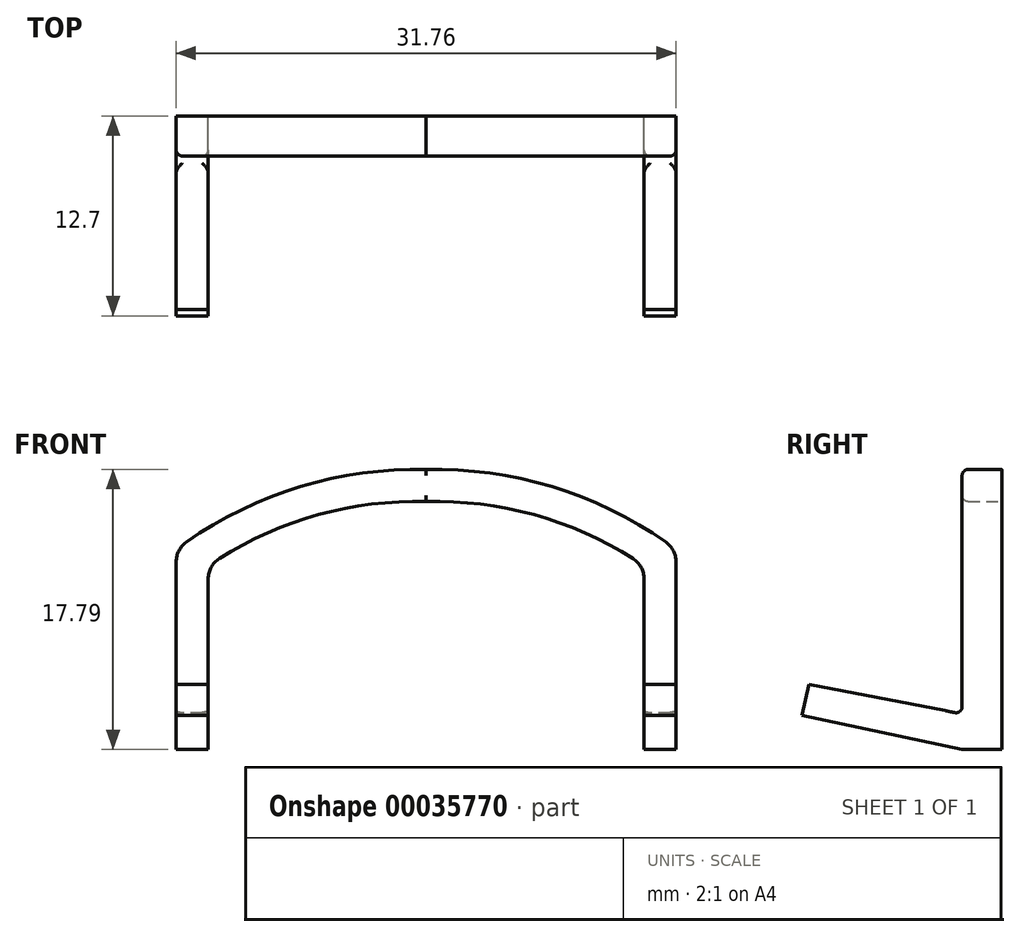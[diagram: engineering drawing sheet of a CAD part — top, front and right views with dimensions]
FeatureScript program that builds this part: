
annotation { "Feature Type Name" : "Feature", "Feature Type Description" : "" }
export const myFeature = defineFeature(function(context is Context, id is Id, definition is map)
    precondition{}
    {
        {
            var Q0;
            Q0=qCreatedBy(makeId("Front.planeOp"),FACE);
            var sketch = newSketch(context, id + "F0", { "sketchPlane" : qUnion([Q0])});
            skLineSegment(sketch, "E0", {"start": v(0, 0) * mm, "end": v(0, 38.1) * mm, "construction": true});
            skLineSegment(sketch, "E1", {"start": v(-15.88, 11.92) * mm, "end": v(-15.88, 0) * mm});
            skLineSegment(sketch, "E2", {"start": v(-15.88, 0) * mm, "end": v(-13.84, 0) * mm});
            skLineSegment(sketch, "E3", {"start": v(-13.84, 0) * mm, "end": v(-13.84, 10.84) * mm});
            skArc(sketch, "E4", {"start": v(0, 17.78) * mm, "mid": v(-7.98, 16.7) * mm, "end": v(-15.23, 13.17) * mm});
            skArc(sketch, "E5.0", {"start": v(0, 15.75) * mm, "mid": v(-6.84, 14.91) * mm, "end": v(-13.13, 12.12) * mm});
            skArc(sketch, "E6.filletArc", {"start": v(-13.13, 12.12) * mm, "mid": v(-13.65, 11.57) * mm, "end": v(-13.84, 10.84) * mm});
            skPoint(sketch, "E7.visualSharp", {"position": v(-15.88, 12.7) * mm});
            skArc(sketch, "E7.filletArc", {"start": v(-15.23, 13.17) * mm, "mid": v(-15.7, 12.63) * mm, "end": v(-15.88, 11.92) * mm});
            skArc(sketch, "E8.MirrorCS", {"start": v(13.13, 12.12) * mm, "mid": v(13.65, 11.57) * mm, "end": v(13.84, 10.84) * mm});
            skArc(sketch, "E9.MirrorCS", {"start": v(15.23, 13.17) * mm, "mid": v(15.7, 12.63) * mm, "end": v(15.88, 11.92) * mm});
            skLineSegment(sketch, "E10.MirrorCS", {"start": v(15.88, 0) * mm, "end": v(13.84, 0) * mm});
            skArc(sketch, "E11.MirrorCS", {"start": v(0, 17.78) * mm, "mid": v(7.98, 16.7) * mm, "end": v(15.23, 13.17) * mm});
            skPoint(sketch, "E12.MirrorP", {"position": v(15.88, 12.7) * mm});
            skLineSegment(sketch, "E13.MirrorCS", {"start": v(15.88, 11.92) * mm, "end": v(15.88, 0) * mm});
            skLineSegment(sketch, "E14.MirrorCS", {"start": v(13.84, 0) * mm, "end": v(13.84, 10.84) * mm});
            skArc(sketch, "E15.MirrorCS", {"start": v(0, 15.75) * mm, "mid": v(6.84, 14.91) * mm, "end": v(13.13, 12.12) * mm});
            skSolve(sketch);
        }
        {
            var Q0;
            Q0 = qSketchRegion(id + "F0", true);
            extrude(context, id + "F1", {"entities" : qUnion([Q0]), "depth" : 2.54 * mm});
        }
        {
            var Q0;
            Q0=qCreatedBy(makeId("Right.planeOp"),FACE);
            var sketch = newSketch(context, id + "F2", { "sketchPlane" : qUnion([Q0])});
            skLineSegment(sketch, "E16.0", {"start": v(-2.54, 2.25) * mm, "end": v(-2.54, 0) * mm});
            skLineSegment(sketch, "E17", {"start": v(-2.54, 0) * mm, "end": v(-12.7, 2.16) * mm});
            skLineSegment(sketch, "E18", {"start": v(-2.54, 2.25) * mm, "end": v(-12.28, 4.15) * mm});
            skLineSegment(sketch, "E19", {"start": v(-12.28, 4.15) * mm, "end": v(-12.7, 2.16) * mm});
            skPoint(sketch, "E20.orphan", {"position": v(-2.54, 11.92) * mm});
            skLineSegment(sketch, "E21", {"start": v(-2.54, 0) * mm, "end": v(-11.31, 0) * mm, "construction": true});
            skSolve(sketch);
        }
        {
            var Q0;
            Q0 = qSketchRegion(id + "F2", true);
            var Q1;
            Q1=makeQuery(id+"F1.opExtrude","SWEPT_FACE",FACE,{"disambiguationData":[OSD([sQuery(id+"F0.wireOp",EDGE,"E13.MirrorCS")])]});
            var Q2;
            Q2=makeQuery(id+"F1.opExtrude","SWEPT_FACE",FACE,{"disambiguationData":[OSD([sQuery(id+"F0.wireOp",EDGE,"E1")])]});
            extrude(context, id + "F3", {"entities" : qUnion([Q0]), "operationType" : NewBodyOperationType.ADD, "endBound" : BoundingType.UP_TO_SURFACE, "endBoundEntityFace" : qUnion([Q1]), "depth" : 25.4 * mm, "hasSecondDirection" : true, "secondDirectionBound" : SecondDirectionBoundingType.UP_TO_SURFACE, "secondDirectionOppositeDirection" : true, "secondDirectionBoundEntityFace" : qUnion([Q2]), "secondDirectionDepth" : 25.4 * mm});
        }
        {
            var Q0;
            Q0=qCreatedBy(makeId("Front.planeOp"),FACE);
            var sketch = newSketch(context, id + "F4", { "sketchPlane" : qUnion([Q0])});
            skLineSegment(sketch, "E22.0", {"start": v(-13.84, 2.25) * mm, "end": v(-13.84, 10.84) * mm});
            skLineSegment(sketch, "E23.1", {"start": v(13.84, 2.25) * mm, "end": v(13.84, 10.84) * mm});
            skLineSegment(sketch, "E24", {"start": v(-13.84, 10.84) * mm, "end": v(13.84, 10.84) * mm});
            skLineSegment(sketch, "E25", {"start": v(13.84, -2.66) * mm, "end": v(-12.06, -2.66) * mm});
            skLineSegment(sketch, "E26", {"start": v(-13.84, 2.25) * mm, "end": v(-13.84, -2.66) * mm});
            skLineSegment(sketch, "E27", {"start": v(13.84, 2.25) * mm, "end": v(13.84, -2.66) * mm});
            skLineSegment(sketch, "E28", {"start": v(-12.06, -2.66) * mm, "end": v(-13.84, -2.66) * mm});
            skSolve(sketch);
        }
        {
            var Q0;
            Q0 = qSketchRegion(id + "F4", true);
            extrude(context, id + "F5", {"entities" : qUnion([Q0]), "operationType" : NewBodyOperationType.REMOVE, "depth" : 25.4 * mm});
        }
        {
            var Q0;
            Q0=makeQuery(id+"F1.opExtrude","CAP_FACE",FACE,{"disambiguationData":[OSD([sQuery(id+"F0.wireOp",EDGE,"E1"),sQuery(id+"F0.wireOp",EDGE,"E2"),sQuery(id+"F0.wireOp",EDGE,"E3"),sQuery(id+"F0.wireOp",EDGE,"E4"),sQuery(id+"F0.wireOp",EDGE,"E5.0"),sQuery(id+"F0.wireOp",EDGE,"E6.filletArc"),sQuery(id+"F0.wireOp",EDGE,"E7.filletArc"),sQuery(id+"F0.wireOp",EDGE,"E8.MirrorCS"),sQuery(id+"F0.wireOp",EDGE,"E9.MirrorCS"),sQuery(id+"F0.wireOp",EDGE,"E10.MirrorCS"),sQuery(id+"F0.wireOp",EDGE,"E11.MirrorCS"),sQuery(id+"F0.wireOp",EDGE,"E13.MirrorCS"),sQuery(id+"F0.wireOp",EDGE,"E14.MirrorCS"),sQuery(id+"F0.wireOp",EDGE,"E15.MirrorCS")])],"isStart":false});
            fillet(context, id + "F6", {"entities" : qUnion([Q0]), "radius" : 0.38 * mm, "tangentPropagation" : true, "allowEdgeOverflow" : false});
        }
    });
